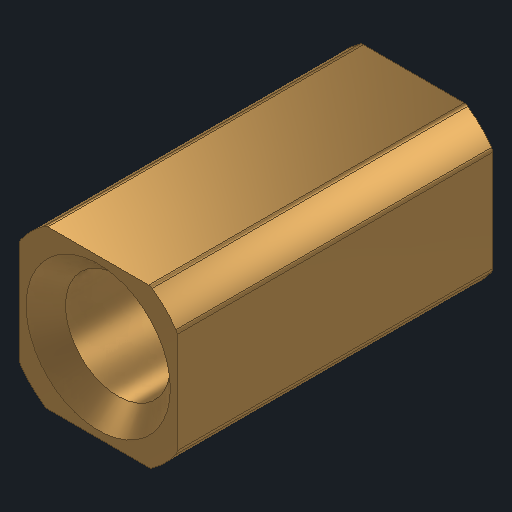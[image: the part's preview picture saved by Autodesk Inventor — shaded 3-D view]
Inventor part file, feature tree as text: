
AUTODESK INVENTOR PART (.ipt)
format: ipt  version: 2025 (Build 290162000, 162)  size: 160,768 bytes
history: native  units: in
note: dims shown in document units (in); Inventor stores cm internally (conversion verified against a paired STEP export)
features: other x3, sketch x2
ambient origin geometry x8: Origin, YZ Plane, XZ Plane, XY Plane, X Axis, Y Axis, Z Axis, Center Point
bodies: Solid1 (feature_tree)
feature tree (5):
  other  "HS Shaft Adapter Circle.ipt"
  other  "Solid1::HS Shaft Adapter Circle.ipt"
  other  "TaggingFeature1"
  sketch  "Sketch1"  dims[d0=0.3937in]
  sketch  "Sketch2"
